# Revit family: NBS_PineappleContracts_DmstcChrs_RynoTubChair
name_source: partatom
category: Furniture
revit_build: Autodesk Revit 2017 (Build: 20171027_0315(x64)
units: mm (PartAtom-declared; Revit-internal decimal feet)

## family parameters
Always vertical = Yes
Cut with Voids When Loaded = No
Room Calculation Point = No
Shared = No
Work Plane-Based = No

## types (1)
- Ryno Tub Chair
    AssetType = Moveable
    BIMObjectName = NBS_PineappleContracts_DomesticChairs_RynoTubChair
    Category = Pr_40_50_12_22:Dining chairs
    ChairBodyMaterial = NBS_Concept
    CodePerformance = UL 94 HB, BS EN 16139:2013 level 2, BS 5852:2006 source 5
    Color = Epic blue, icon purple, blaze orange, vegas yellow, lime green, cool green, alpine white, granite, moonwalk grey, thunder grey, black
    Description = Ryno tub chair is designed for challenging and high traffic areas. It is ideal for indoor as well as outdoor use [when used without seat pad]
    DurationUnit = year
    ExpectedLife = Lifetime [except seat pad]
    Features = Anti-microbial polyethylene additive, UV stabilised and water-resistant, Heavy duty linking and floor anchor brackets available, Optional matching upholstered seat
    Finish = Shot-peen surface finish
    FramesFinish = Shot-peen surface finish
    FramesMaterial = Polyethylene
    HighestSeatingHeight = 0 mm  [stored 0 ft]
    IfcExportAs = IfcFurnitureType
    IfcExportType = CHAIR
    LowestSeatingHeight = 0 mm  [stored 0 ft]
    ManufacturerName = Pineapple Contracts
    ManufacturerURL = www.pineapplecontracts.com/
    Material = Chair - Polyethylene, Seat pad - Plywood, foam, fabric
    ModelReference = Ryno Tub Chair
    NBSCertification = www.nationalbimlibrary.com/cert/us2a43uu
    NBSDescription = Domestic chairs
    NBSReference = 45-35-20/365
    Name = DomesticChairs_RynoTubChair_PineappleContracts
    NominalHeight = 802 mm  [stored 2.63123 ft]
    NominalLength = 674 mm  [stored 2.21129 ft]
    NominalWidth = 666 mm  [stored 2.18504 ft]
    ProductInformation = www.pineapplecontracts.com/products/challenging-environment-furniture/10/ryno-tub-chair/271
    SeatingHeight = 430 mm
    SeatsAndBacksMaterial = Polyethylene
    Size = 680 x 666 x 803 mm
    SustainabilityPerformance = 100% recyclable; excluding seat pad
    Uniclass2015Code = Pr_40_50_12_22
    Uniclass2015Title = Dining chairs
    Uniclass2015Version = Products v1.8
    Version = 3
    WarrantyDescription = Ryno tub supplied by pineapple contracts is guaranteed with lifetime warranty against faulty materials or workmanship
    WarrantyDurationUnit = year

note: [stored X ft] marks values corroborated as IEEE doubles in the binary element streams (Revit-internal decimal feet)

## geometry (parser evidence)
native form markers: Sweep x2
no freeform markers — native parametric forms only
